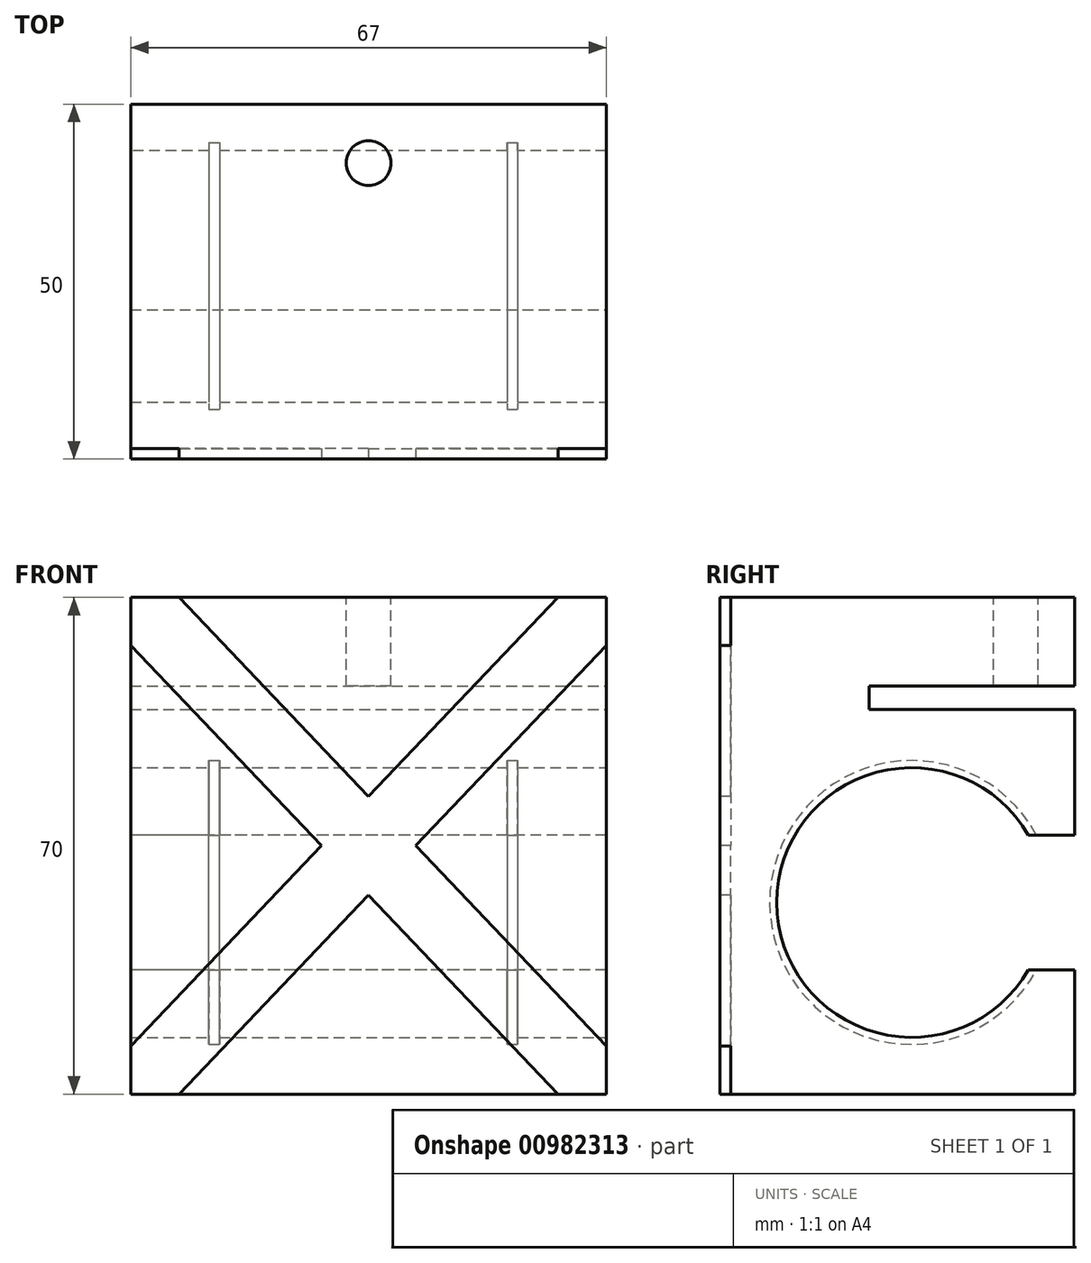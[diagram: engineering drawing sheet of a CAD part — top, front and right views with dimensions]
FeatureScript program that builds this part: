
annotation { "Feature Type Name" : "Feature", "Feature Type Description" : "" }
export const myFeature = defineFeature(function(context is Context, id is Id, definition is map)
    precondition{}
    {
        {
            var Q0;
            Q0=qCreatedBy(makeId("Front.planeOp"),FACE);
            var sketch = newSketch(context, id + "F0", { "sketchPlane" : qUnion([Q0])});
            skLineSegment(sketch, "E0.bottom", {"start": v(-67, 70) * mm, "end": v(0, 70) * mm});
            skLineSegment(sketch, "E0.top", {"start": v(-67, 0) * mm, "end": v(0, 0) * mm});
            skLineSegment(sketch, "E0.left", {"start": v(-67, 70) * mm, "end": v(-67, 0) * mm});
            skLineSegment(sketch, "E0.right", {"start": v(0, 70) * mm, "end": v(0, 0) * mm});
            skSolve(sketch);
        }
        {
            var Q0;
            Q0=makeQuery(id+"F0.imprint","IMPRINT",FACE,{"disambiguationData":[TD([[makeQuery(id+"F0.imprint","IMPRINT",EDGE,{"derivedFrom":sQuery(id+"F0.wireOp",EDGE,"E0.bottom")}),-1.0]])]});
            extrude(context, id + "F1", {"entities" : qUnion([Q0]), "oppositeDirection" : true, "depth" : 50 * mm, "offsetDistance" : 25 * mm});
        }
        {
            var Q0;
            Q0=makeQuery(id+"F1.opExtrude","CAP_FACE",FACE,{"disambiguationData":[OSD([sQuery(id+"F0.wireOp",EDGE,"E0.bottom"),sQuery(id+"F0.wireOp",EDGE,"E0.top"),sQuery(id+"F0.wireOp",EDGE,"E0.left"),sQuery(id+"F0.wireOp",EDGE,"E0.right")])],"isStart":true});
            var sketch = newSketch(context, id + "F2", { "sketchPlane" : qUnion([Q0])});
            skLineSegment(sketch, "E1", {"start": v(-33.5, 70) * mm, "end": v(-33.5, 0) * mm, "construction": true});
            skLineSegment(sketch, "E2", {"start": v(-67, 35) * mm, "end": v(0, 35) * mm, "construction": true});
            skLineSegment(sketch, "E3", {"start": v(-67, 0) * mm, "end": v(-67, 6.8) * mm});
            skLineSegment(sketch, "E4", {"start": v(-67, 6.8) * mm, "end": v(-40.13, 35) * mm});
            skLineSegment(sketch, "E5", {"start": v(-6.8, 70) * mm, "end": v(0, 70) * mm});
            skLineSegment(sketch, "E6", {"start": v(0, 70) * mm, "end": v(0, 63.2) * mm});
            skLineSegment(sketch, "E7", {"start": v(0, 63.2) * mm, "end": v(-26.87, 35) * mm});
            skLineSegment(sketch, "E8", {"start": v(-60.2, 0) * mm, "end": v(-67, 0) * mm});
            skLineSegment(sketch, "E9.MirrorCS", {"start": v(-67, 63.2) * mm, "end": v(-40.13, 35) * mm});
            skLineSegment(sketch, "E10.MirrorCS", {"start": v(0, 6.8) * mm, "end": v(-26.87, 35) * mm});
            skLineSegment(sketch, "E11.MirrorCS", {"start": v(-6.8, 0) * mm, "end": v(0, 0) * mm});
            skLineSegment(sketch, "E12.MirrorCS", {"start": v(0, 0) * mm, "end": v(0, 6.8) * mm});
            skLineSegment(sketch, "E13.MirrorCS", {"start": v(-67, 70) * mm, "end": v(-67, 63.2) * mm});
            skLineSegment(sketch, "E14.MirrorCS", {"start": v(-60.2, 70) * mm, "end": v(-67, 70) * mm});
            skLineSegment(sketch, "E15.trimOffspring", {"start": v(-33.5, 28.04) * mm, "end": v(-60.2, 0) * mm});
            skLineSegment(sketch, "E16.trimOffspring", {"start": v(-33.5, 41.96) * mm, "end": v(-60.2, 70) * mm});
            skLineSegment(sketch, "E17.trimOffspring", {"start": v(-33.5, 41.96) * mm, "end": v(-6.8, 70) * mm});
            skLineSegment(sketch, "E18.trimOffspring", {"start": v(-33.5, 28.04) * mm, "end": v(-6.8, 0) * mm});
            skSolve(sketch);
        }
        {
            var Q0;
            Q0=makeQuery(id+"F2.imprint","IMPRINT",FACE,{"disambiguationData":[TD([[makeQuery(id+"F2.imprint","IMPRINT",EDGE,{"derivedFrom":sQuery(id+"F2.wireOp",EDGE,"E3")}),1.0]])]});
            extrude(context, id + "F3", {"entities" : qUnion([Q0]), "operationType" : NewBodyOperationType.REMOVE, "oppositeDirection" : true, "depth" : 1.5 * mm, "offsetDistance" : 25 * mm});
        }
        {
            var Q0;
            Q0=makeQuery(id+"F1.opExtrude","SWEPT_FACE",FACE,{"disambiguationData":[OSD([sQuery(id+"F0.wireOp",EDGE,"E0.right")])]});
            var sketch = newSketch(context, id + "F4", { "sketchPlane" : qUnion([Q0])});
            skCircle(sketch, "E19", {"center": v(27, 27) * mm, "radius": 19 * mm});
            skSolve(sketch);
        }
        {
            var Q0;
            Q0=makeQuery(id+"F4.imprint","IMPRINT",FACE,{"disambiguationData":[TD([[makeQuery(id+"F4.imprint","IMPRINT",EDGE,{"derivedFrom":sQuery(id+"F4.wireOp",EDGE,"E19")}),1.0]])]});
            extrude(context, id + "F5", {"entities" : qUnion([Q0]), "operationType" : NewBodyOperationType.REMOVE, "endBound" : BoundingType.THROUGH_ALL, "oppositeDirection" : true, "depth" : 25 * mm, "offsetDistance" : 25 * mm});
        }
        {
            var Q0;
            Q0=makeQuery(id+"F1.opExtrude","SWEPT_FACE",FACE,{"disambiguationData":[OSD([sQuery(id+"F0.wireOp",EDGE,"E0.bottom")])]});
            var sketch = newSketch(context, id + "F6", { "sketchPlane" : qUnion([Q0])});
            skCircle(sketch, "E20", {"center": v(-33.5, 41.7) * mm, "radius": 3.15 * mm});
            skSolve(sketch);
        }
        {
            var Q0;
            Q0=makeQuery(id+"F1.opExtrude","SWEPT_FACE",FACE,{"disambiguationData":[OSD([sQuery(id+"F0.wireOp",EDGE,"E0.right")])]});
            var sketch = newSketch(context, id + "F7", { "sketchPlane" : qUnion([Q0])});
            skLineSegment(sketch, "E21.bottom", {"start": v(50, 57.5) * mm, "end": v(21, 57.5) * mm});
            skLineSegment(sketch, "E21.top", {"start": v(50, 54.2) * mm, "end": v(21, 54.2) * mm});
            skLineSegment(sketch, "E21.left", {"start": v(50, 57.5) * mm, "end": v(50, 54.2) * mm});
            skLineSegment(sketch, "E21.right", {"start": v(21, 57.5) * mm, "end": v(21, 54.2) * mm});
            skSolve(sketch);
        }
        {
            var Q0;
            Q0 = qSketchRegion(id + "F7", true);
            extrude(context, id + "F8", {"entities" : qUnion([Q0]), "operationType" : NewBodyOperationType.REMOVE, "endBound" : BoundingType.THROUGH_ALL, "oppositeDirection" : true, "depth" : 25 * mm, "offsetDistance" : 25 * mm});
        }
        {
            var Q0;
            Q0=makeQuery(id+"F6.imprint","IMPRINT",FACE,{"disambiguationData":[TD([[makeQuery(id+"F6.imprint","IMPRINT",EDGE,{"derivedFrom":sQuery(id+"F6.wireOp",EDGE,"E20")}),1.0]])]});
            var Q1;
            Q1=makeQuery(id+"F8.boolean.opBoolean","COPY",FACE,{"derivedFrom":makeQuery(id+"F8.opExtrude","SWEPT_FACE",FACE,{"disambiguationData":[OSD([sQuery(id+"F7.wireOp",EDGE,"E21.bottom")])]})});
            extrude(context, id + "F9", {"entities" : qUnion([Q0]), "operationType" : NewBodyOperationType.REMOVE, "endBound" : BoundingType.UP_TO_SURFACE, "oppositeDirection" : true, "depth" : 25 * mm, "endBoundEntityFace" : qUnion([Q1]), "offsetDistance" : 25 * mm});
        }
        {
            var Q0;
            Q0=makeQuery(id+"F1.opExtrude","SWEPT_FACE",FACE,{"disambiguationData":[OSD([sQuery(id+"F0.wireOp",EDGE,"E0.right")])]});
            cPlane(context, id + "F10", {"entities" : qUnion([Q0]), "cplaneType" : CPlaneType.OFFSET, "offset" : 12.5 * mm, "oppositeDirection" : true, "width" : 150 * mm, "height" : 150 * mm});
        }
        {
            var Q0;
            Q0=qCreatedBy(id+"F10.planeOp",FACE);
            var sketch = newSketch(context, id + "F11", { "sketchPlane" : qUnion([Q0])});
            skCircle(sketch, "E22", {"center": v(27, 27) * mm, "radius": 20 * mm});
            skSolve(sketch);
        }
        {
            var Q0;
            Q0=makeQuery(id+"F11.imprint","IMPRINT",FACE,{"disambiguationData":[TD([[makeQuery(id+"F11.imprint","IMPRINT",EDGE,{"derivedFrom":sQuery(id+"F11.wireOp",EDGE,"E22")}),1.0]])]});
            extrude(context, id + "F12", {"entities" : qUnion([Q0]), "operationType" : NewBodyOperationType.REMOVE, "oppositeDirection" : true, "depth" : 1.5 * mm, "offsetDistance" : 25 * mm});
        }
        {
            var Q0;
            Q0=makeQuery(id+"F1.opExtrude","SWEPT_FACE",FACE,{"disambiguationData":[OSD([sQuery(id+"F0.wireOp",EDGE,"E0.left")])]});
            cPlane(context, id + "F13", {"entities" : qUnion([Q0]), "cplaneType" : CPlaneType.OFFSET, "offset" : 12.5 * mm, "oppositeDirection" : true, "width" : 150 * mm, "height" : 150 * mm});
        }
        {
            var Q0;
            Q0=qCreatedBy(id+"F13.planeOp",FACE);
            var sketch = newSketch(context, id + "F14", { "sketchPlane" : qUnion([Q0])});
            skCircle(sketch, "E23", {"center": v(-27, 27) * mm, "radius": 20 * mm});
            skSolve(sketch);
        }
        {
            var Q0;
            Q0=makeQuery(id+"F14.imprint","IMPRINT",FACE,{"disambiguationData":[TD([[makeQuery(id+"F14.imprint","IMPRINT",EDGE,{"derivedFrom":sQuery(id+"F14.wireOp",EDGE,"E23")}),1.0]])]});
            extrude(context, id + "F15", {"entities" : qUnion([Q0]), "operationType" : NewBodyOperationType.REMOVE, "depth" : 1.5 * mm, "offsetDistance" : 25 * mm});
        }
        {
            var Q0;
            Q0=makeQuery(id+"F1.opExtrude","SWEPT_FACE",FACE,{"disambiguationData":[OSD([sQuery(id+"F0.wireOp",EDGE,"E0.left")])]});
            var sketch = newSketch(context, id + "F16", { "sketchPlane" : qUnion([Q0])});
            skLineSegment(sketch, "E24.bottom", {"start": v(-54.87, 36.5) * mm, "end": v(-41.77, 36.5) * mm});
            skLineSegment(sketch, "E24.top", {"start": v(-54.87, 17.5) * mm, "end": v(-41.77, 17.5) * mm});
            skLineSegment(sketch, "E24.left", {"start": v(-54.87, 36.5) * mm, "end": v(-54.87, 17.5) * mm});
            skLineSegment(sketch, "E24.right", {"start": v(-41.77, 36.5) * mm, "end": v(-41.77, 17.5) * mm});
            skSolve(sketch);
        }
        {
            var Q0;
            {var subQ0=sQuery(id+"F16.wireOp",EDGE,"E24.bottom");var subQ1=sQuery(id+"F0.wireOp",EDGE,"E0.left");var subQ3=makeQuery(id+"F1.opExtrude","SWEPT_FACE",FACE,{"disambiguationData":[OSD([subQ1])]});var subQ6=makeQuery(id+"F5.boolean.opBoolean","INTERSECT",EDGE,{"derivedFrom":[subQ3,makeQuery(id+"F5.opExtrude","SWEPT_FACE",FACE,{"disambiguationData":[OSD([sQuery(id+"F4.wireOp",EDGE,"E19")])]})]});var subQ7=makeQuery(id+"F16.imprint","INTERSECT",VERTEX,{"derivedFrom":[subQ6,subQ0]});Q0=makeQuery(id+"F16.imprint","IMPRINT",FACE,{"disambiguationData":[TD([[makeQuery(id+"F16.imprint","IMPRINT",EDGE,{"disambiguationData":[TD([[subQ7,-1.0]])],"derivedFrom":subQ6}),-1.0]])]});}
            extrude(context, id + "F17", {"entities" : qUnion([Q0]), "operationType" : NewBodyOperationType.REMOVE, "endBound" : BoundingType.THROUGH_ALL, "oppositeDirection" : true, "depth" : 25 * mm, "offsetDistance" : 25 * mm});
        }
    });
